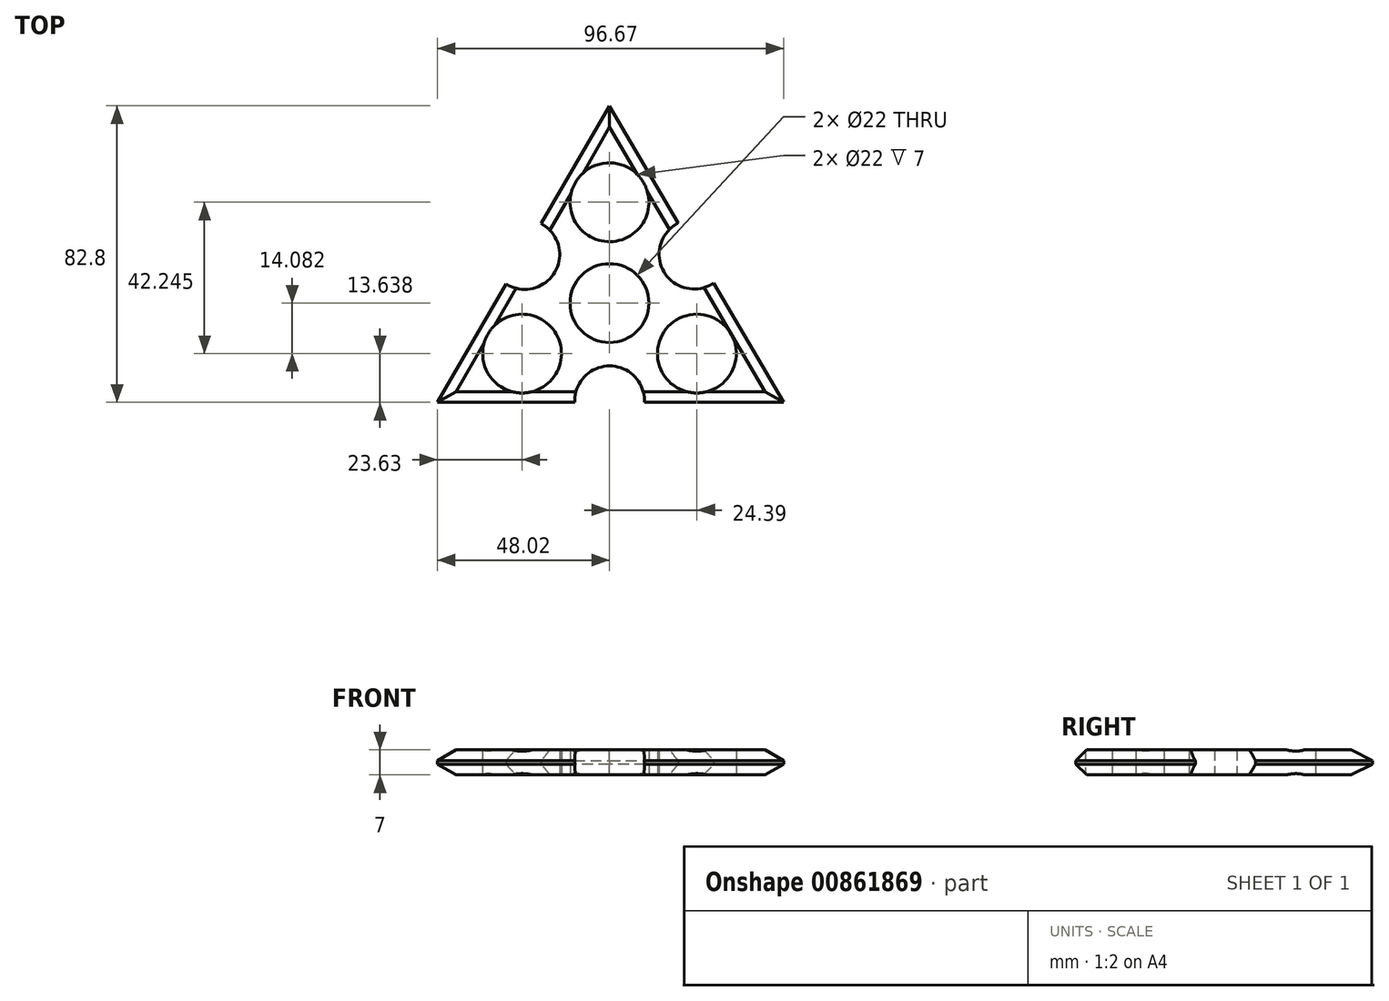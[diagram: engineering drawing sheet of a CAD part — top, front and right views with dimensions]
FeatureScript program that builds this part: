
annotation { "Feature Type Name" : "Feature", "Feature Type Description" : "" }
export const myFeature = defineFeature(function(context is Context, id is Id, definition is map)
    precondition{}
    {
        {
            var Q0;
            Q0=qCreatedBy(makeId("Top.planeOp"),FACE);
            var sketch = newSketch(context, id + "F0", { "sketchPlane" : qUnion([Q0])});
            skCircle(sketch, "E0", {"center": v(0, 0) * mm, "radius": 11 * mm});
            skCircle(sketch, "E1", {"center": v(0, 28.16) * mm, "radius": 11 * mm});
            skCircle(sketch, "E2.1.0", {"center": v(-24.4, -14.08) * mm, "radius": 11 * mm});
            skCircle(sketch, "E2.2.0", {"center": v(24.4, -14.08) * mm, "radius": 11 * mm});
            skPoint(sketch, "E3.center.orphan", {"position": v(-23.65, 13.6) * mm});
            skPoint(sketch, "E2.1.1.start.orphan", {"position": v(-35.82, -7.48) * mm});
            skPoint(sketch, "E4.end.orphan", {"position": v(-11.48, 34.69) * mm});
            skLineSegment(sketch, "E5", {"start": v(0, 55.08) * mm, "end": v(-19.07, 22.2) * mm});
            skLineSegment(sketch, "E6", {"start": v(-48.02, -27.72) * mm, "end": v(-9.69, -27.72) * mm});
            skLineSegment(sketch, "E7", {"start": v(48.65, -27.72) * mm, "end": v(29.07, 5.61) * mm});
            skArc(sketch, "E8", {"start": v(-28.84, 5.35) * mm, "mid": v(-15.22, 8.71) * mm, "end": v(-19.07, 22.2) * mm});
            skArc(sketch, "E9.1.0", {"start": v(9.78, -27.72) * mm, "mid": v(0.04, -17.54) * mm, "end": v(-9.69, -27.72) * mm});
            skArc(sketch, "E9.2.0", {"start": v(19.22, 22.38) * mm, "mid": v(15.2, 8.74) * mm, "end": v(29.07, 5.61) * mm});
            skLineSegment(sketch, "E10.trimOffspring", {"start": v(-28.84, 5.35) * mm, "end": v(-48.02, -27.72) * mm});
            skLineSegment(sketch, "E11.trimOffspring", {"start": v(19.22, 22.38) * mm, "end": v(0, 55.08) * mm});
            skLineSegment(sketch, "E12.trimOffspring", {"start": v(9.78, -27.72) * mm, "end": v(48.65, -27.72) * mm});
            skSolve(sketch);
        }
        {
            var Q0;
            Q0=makeQuery(id+"F0.imprint","IMPRINT",FACE,{"disambiguationData":[TD([[makeQuery(id+"F0.imprint","IMPRINT",EDGE,{"derivedFrom":sQuery(id+"F0.wireOp",EDGE,"E0")}),-1.0]])]});
            extrude(context, id + "F1", {"entities" : qUnion([Q0]), "depth" : 7 * mm, "offsetDistance" : 25 * mm});
        }
        {
            var Q0;
            Q0=makeQuery(id+"F1.opExtrude","CAP_EDGE",EDGE,{"disambiguationData":[OSD([sQuery(id+"F0.wireOp",EDGE,"E5")])],"isStart":false});
            var Q1;
            Q1=makeQuery(id+"F1.opExtrude","CAP_EDGE",EDGE,{"disambiguationData":[OSD([sQuery(id+"F0.wireOp",EDGE,"E11.trimOffspring")])],"isStart":false});
            var Q2;
            Q2=makeQuery(id+"F1.opExtrude","CAP_EDGE",EDGE,{"disambiguationData":[OSD([sQuery(id+"F0.wireOp",EDGE,"E10.trimOffspring")])],"isStart":false});
            var Q3;
            Q3=makeQuery(id+"F1.opExtrude","CAP_EDGE",EDGE,{"disambiguationData":[OSD([sQuery(id+"F0.wireOp",EDGE,"E6")])],"isStart":false});
            var Q4;
            Q4=makeQuery(id+"F1.opExtrude","CAP_EDGE",EDGE,{"disambiguationData":[OSD([sQuery(id+"F0.wireOp",EDGE,"E12.trimOffspring")])],"isStart":false});
            var Q5;
            Q5=makeQuery(id+"F1.opExtrude","CAP_EDGE",EDGE,{"disambiguationData":[OSD([sQuery(id+"F0.wireOp",EDGE,"E7")])],"isStart":false});
            chamfer(context, id + "F2", {"entities" : qUnion([Q0, Q1, Q2, Q3, Q4, Q5]), "width" : 3 * mm, "tangentPropagation" : true});
        }
        {
            var Q0;
            Q0=makeQuery(id+"F1.opExtrude","CAP_EDGE",EDGE,{"disambiguationData":[OSD([sQuery(id+"F0.wireOp",EDGE,"E5")])],"isStart":true});
            var Q1;
            Q1=makeQuery(id+"F1.opExtrude","CAP_EDGE",EDGE,{"disambiguationData":[OSD([sQuery(id+"F0.wireOp",EDGE,"E10.trimOffspring")])],"isStart":true});
            var Q2;
            Q2=makeQuery(id+"F1.opExtrude","CAP_EDGE",EDGE,{"disambiguationData":[OSD([sQuery(id+"F0.wireOp",EDGE,"E6")])],"isStart":true});
            var Q3;
            Q3=makeQuery(id+"F1.opExtrude","CAP_EDGE",EDGE,{"disambiguationData":[OSD([sQuery(id+"F0.wireOp",EDGE,"E12.trimOffspring")])],"isStart":true});
            var Q4;
            Q4=makeQuery(id+"F1.opExtrude","CAP_EDGE",EDGE,{"disambiguationData":[OSD([sQuery(id+"F0.wireOp",EDGE,"E7")])],"isStart":true});
            var Q5;
            Q5=makeQuery(id+"F1.opExtrude","CAP_EDGE",EDGE,{"disambiguationData":[OSD([sQuery(id+"F0.wireOp",EDGE,"E11.trimOffspring")])],"isStart":true});
            chamfer(context, id + "F3", {"entities" : qUnion([Q0, Q1, Q2, Q3, Q4, Q5]), "width" : 3 * mm, "tangentPropagation" : true});
        }
    });
